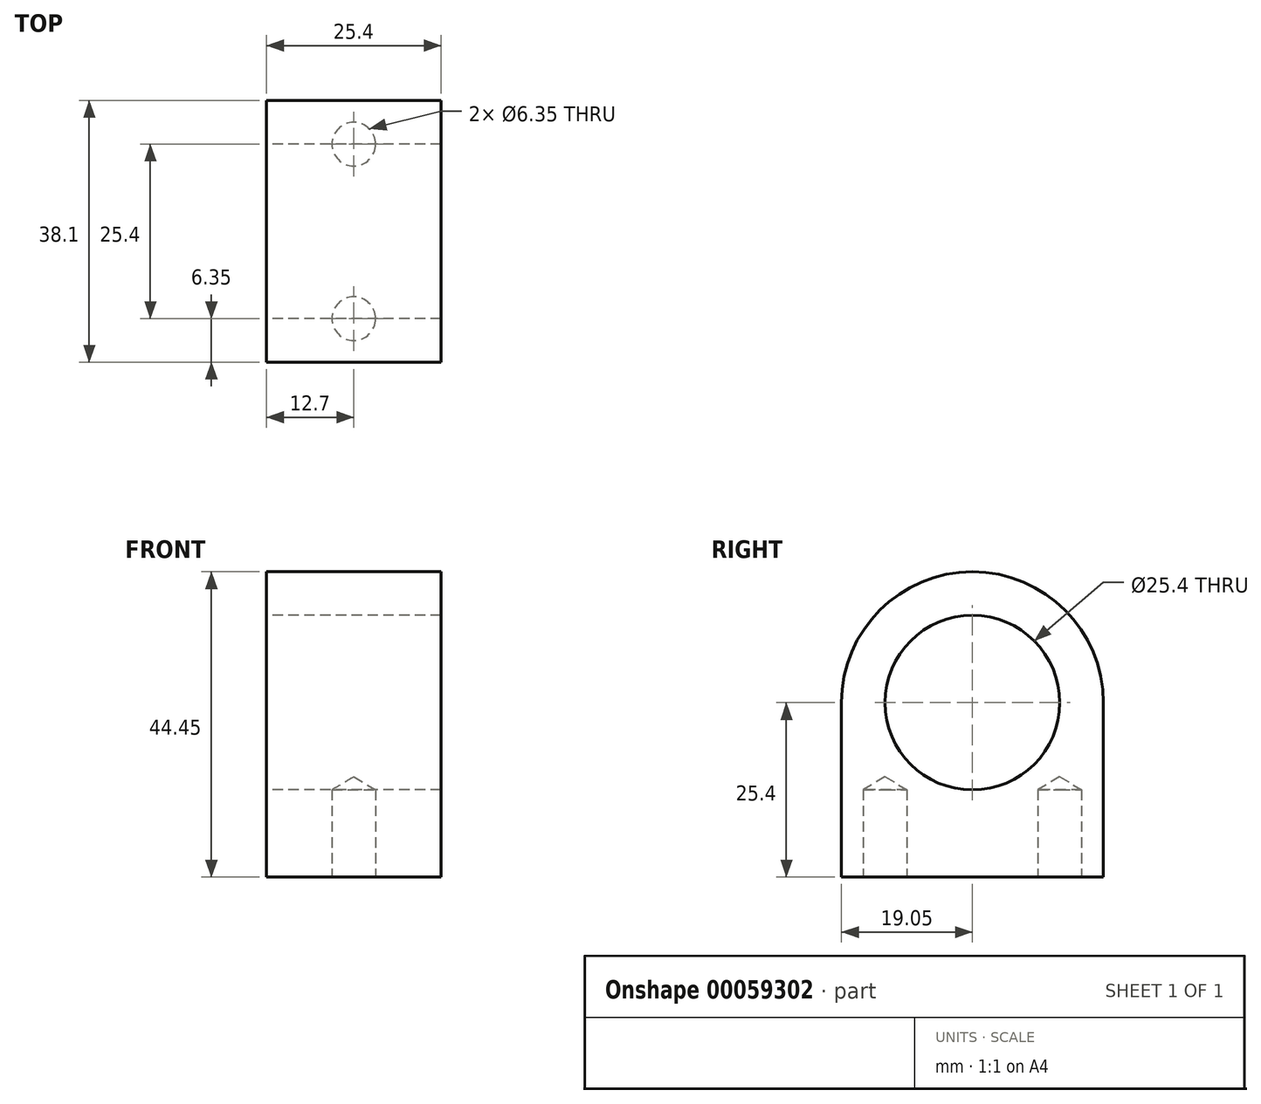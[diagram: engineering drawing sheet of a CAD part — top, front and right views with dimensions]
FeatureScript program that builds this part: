
annotation { "Feature Type Name" : "Feature", "Feature Type Description" : "" }
export const myFeature = defineFeature(function(context is Context, id is Id, definition is map)
    precondition{}
    {
        {
            var Q0;
            Q0=qCreatedBy(makeId("Right.planeOp"),FACE);
            var sketch = newSketch(context, id + "F0", { "sketchPlane" : qUnion([Q0])});
            skCircle(sketch, "E0", {"center": v(0, 0) * mm, "radius": 12.7 * mm});
            skArc(sketch, "E1", {"start": v(19.05, 0) * mm, "mid": v(0, 19.05) * mm, "end": v(-19.05, 0) * mm});
            skLineSegment(sketch, "E2", {"start": v(-19.05, 0) * mm, "end": v(-19.05, -25.4) * mm});
            skLineSegment(sketch, "E3", {"start": v(-19.05, -25.4) * mm, "end": v(19.05, -25.4) * mm});
            skLineSegment(sketch, "E4", {"start": v(19.05, -25.4) * mm, "end": v(19.05, 0) * mm});
            skSolve(sketch);
        }
        {
            var Q0;
            Q0=makeQuery(id+"F0.imprint","IMPRINT",FACE,{"disambiguationData":[TD([[makeQuery(id+"F0.imprint","IMPRINT",EDGE,{"derivedFrom":sQuery(id+"F0.wireOp",EDGE,"E0")}),-1.0]])]});
            extrude(context, id + "F1", {"entities" : qUnion([Q0]), "depth" : 25.4 * mm});
        }
        {
            var Q0;
            Q0=makeQuery(id+"F1.opExtrude","SWEPT_FACE",FACE,{"disambiguationData":[OSD([sQuery(id+"F0.wireOp",EDGE,"E3")])]});
            var sketch = newSketch(context, id + "F2", { "sketchPlane" : qUnion([Q0])});
            skCircle(sketch, "E5", {"center": v(12.7, 12.7) * mm, "radius": 3.18 * mm});
            skCircle(sketch, "E6", {"center": v(12.7, -12.7) * mm, "radius": 3.18 * mm});
            skSolve(sketch);
        }
        {
            var Q0;
            Q0=sQuery(id+"F2.wireOp",VERTEX,"E5.center");
            var Q1;
            Q1=sQuery(id+"F2.wireOp",VERTEX,"E6.center");
            var Q2;
            Q2=makeQuery(id+"F1.opExtrude","SWEPT_BODY",BODY,{"disambiguationData":[OSD([sQuery(id+"F0.wireOp",EDGE,"E0"),sQuery(id+"F0.wireOp",EDGE,"E1"),sQuery(id+"F0.wireOp",EDGE,"E2"),sQuery(id+"F0.wireOp",EDGE,"E3"),sQuery(id+"F0.wireOp",EDGE,"E4")])]});
            hole(context, id + "F3", {"style" : HoleStyle.SIMPLE, "holeDiameter" : 6.35 * mm, "endStyle" : HoleEndStyle.BLIND, "holeDepth" : 12.7 * mm, "locations" : qUnion([Q0, Q1]), "scope" : qUnion([Q2])});
        }
    });
